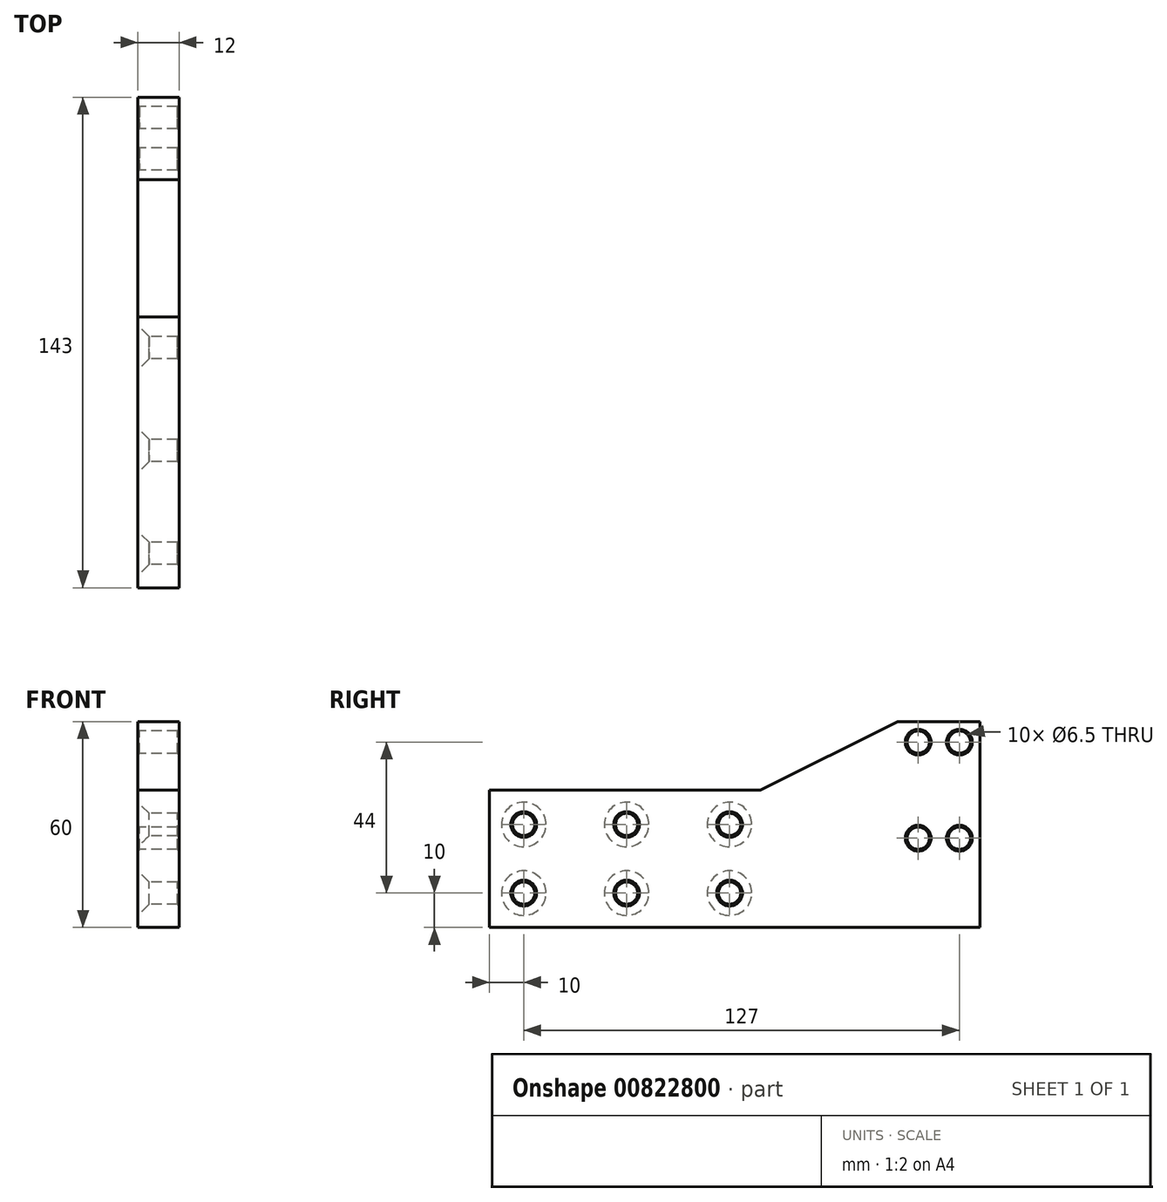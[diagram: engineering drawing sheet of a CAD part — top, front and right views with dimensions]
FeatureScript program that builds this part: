
annotation { "Feature Type Name" : "Feature", "Feature Type Description" : "" }
export const myFeature = defineFeature(function(context is Context, id is Id, definition is map)
    precondition{}
    {
        {
            var Q0;
            Q0=qCreatedBy(makeId("Right.planeOp"),FACE);
            var sketch = newSketch(context, id + "F0", { "sketchPlane" : qUnion([Q0])});
            skLineSegment(sketch, "E0.bottom", {"start": v(-71.5, 20) * mm, "end": v(7.5, 20) * mm});
            skLineSegment(sketch, "E0.top", {"start": v(-71.5, -20) * mm, "end": v(71.5, -20) * mm});
            skLineSegment(sketch, "E0.left", {"start": v(-71.5, 20) * mm, "end": v(-71.5, -20) * mm});
            skLineSegment(sketch, "E0.right", {"start": v(71.5, 20) * mm, "end": v(71.5, -20) * mm});
            skPoint(sketch, "E0.middle", {"position": v(0, 0) * mm});
            skCircle(sketch, "E1", {"center": v(-61.5, 10) * mm, "radius": 3.25 * mm});
            skLineSegment(sketch, "E2", {"start": v(-61.5, 10) * mm, "end": v(-1.5, 10) * mm, "construction": true});
            skCircle(sketch, "E3", {"center": v(-1.5, 10) * mm, "radius": 3.25 * mm});
            skCircle(sketch, "E4", {"center": v(-31.5, 10) * mm, "radius": 3.25 * mm});
            skLineSegment(sketch, "E5", {"start": v(0, 0) * mm, "end": v(-27.42, 0) * mm, "construction": true});
            skCircle(sketch, "E6.MirrorC", {"center": v(-1.5, -10) * mm, "radius": 3.25 * mm});
            skCircle(sketch, "E7.MirrorC", {"center": v(-31.5, -10) * mm, "radius": 3.25 * mm});
            skCircle(sketch, "E8.MirrorC", {"center": v(-61.5, -10) * mm, "radius": 3.25 * mm});
            skLineSegment(sketch, "E9.3", {"start": v(65.5, 34) * mm, "end": v(65.5, 6) * mm, "construction": true});
            skLineSegment(sketch, "E10", {"start": v(47.5, 20) * mm, "end": v(47.5, -20) * mm, "construction": true});
            skCircle(sketch, "E11", {"center": v(65.5, 34) * mm, "radius": 3.25 * mm});
            skCircle(sketch, "E12", {"center": v(53.5, 34) * mm, "radius": 3.25 * mm});
            skCircle(sketch, "E13", {"center": v(53.5, 6) * mm, "radius": 3.25 * mm});
            skCircle(sketch, "E14", {"center": v(65.5, 6) * mm, "radius": 3.25 * mm});
            skLineSegment(sketch, "E15", {"start": v(71.5, 20) * mm, "end": v(71.5, 40) * mm});
            skLineSegment(sketch, "E16", {"start": v(71.5, 40) * mm, "end": v(47.5, 40) * mm});
            skLineSegment(sketch, "E17", {"start": v(47.5, 40) * mm, "end": v(7.5, 20) * mm});
            skLineSegment(sketch, "E18", {"start": v(65.5, 6) * mm, "end": v(53.5, 6) * mm, "construction": true});
            skLineSegment(sketch, "E19", {"start": v(65.5, 34) * mm, "end": v(53.5, 34) * mm, "construction": true});
            skLineSegment(sketch, "E20", {"start": v(53.5, 6) * mm, "end": v(53.5, 34) * mm, "construction": true});
            skSolve(sketch);
        }
        {
            var Q0;
            Q0=qSketchRegion(id+"F0",true);
            extrude(context, id + "F1", {"entities" : qUnion([Q0]), "depth" : 12 * mm, "offsetDistance" : 25 * mm});
        }
        {
            var Q0;
            Q0=makeQuery(id+"F1.opExtrude","CAP_EDGE",EDGE,{"disambiguationData":[OSD([sQuery(id+"F0.wireOp",EDGE,"E3")])],"isStart":true});
            var Q1;
            Q1=makeQuery(id+"F1.opExtrude","CAP_EDGE",EDGE,{"disambiguationData":[OSD([sQuery(id+"F0.wireOp",EDGE,"E6.MirrorC")])],"isStart":true});
            var Q2;
            Q2=makeQuery(id+"F1.opExtrude","CAP_EDGE",EDGE,{"disambiguationData":[OSD([sQuery(id+"F0.wireOp",EDGE,"E7.MirrorC")])],"isStart":true});
            var Q3;
            Q3=makeQuery(id+"F1.opExtrude","CAP_EDGE",EDGE,{"disambiguationData":[OSD([sQuery(id+"F0.wireOp",EDGE,"E4")])],"isStart":true});
            var Q4;
            Q4=makeQuery(id+"F1.opExtrude","CAP_EDGE",EDGE,{"disambiguationData":[OSD([sQuery(id+"F0.wireOp",EDGE,"E8.MirrorC")])],"isStart":true});
            var Q5;
            Q5=makeQuery(id+"F1.opExtrude","CAP_EDGE",EDGE,{"disambiguationData":[OSD([sQuery(id+"F0.wireOp",EDGE,"E1")])],"isStart":true});
            chamfer(context, id + "F2", {"entities" : qUnion([Q0, Q1, Q2, Q3, Q4, Q5]), "width" : 3.25 * mm, "tangentPropagation" : true});
        }
        {
            var Q0;
            Q0=makeQuery(id+"F1.opExtrude","SWEPT_FACE",FACE,{"disambiguationData":[OSD([sQuery(id+"F0.wireOp",EDGE,"E11")])]});
            var Q1;
            Q1=makeQuery(id+"F1.opExtrude","SWEPT_FACE",FACE,{"disambiguationData":[OSD([sQuery(id+"F0.wireOp",EDGE,"E12")])]});
            var Q2;
            Q2=makeQuery(id+"F1.opExtrude","SWEPT_FACE",FACE,{"disambiguationData":[OSD([sQuery(id+"F0.wireOp",EDGE,"E13")])]});
            var Q3;
            Q3=makeQuery(id+"F1.opExtrude","SWEPT_FACE",FACE,{"disambiguationData":[OSD([sQuery(id+"F0.wireOp",EDGE,"E14")])]});
            var Q4;
            Q4=makeQuery(id+"F1.opExtrude","CAP_EDGE",EDGE,{"disambiguationData":[OSD([sQuery(id+"F0.wireOp",EDGE,"E1")])],"isStart":false});
            var Q5;
            Q5=makeQuery(id+"F1.opExtrude","CAP_EDGE",EDGE,{"disambiguationData":[OSD([sQuery(id+"F0.wireOp",EDGE,"E4")])],"isStart":false});
            var Q6;
            Q6=makeQuery(id+"F1.opExtrude","CAP_EDGE",EDGE,{"disambiguationData":[OSD([sQuery(id+"F0.wireOp",EDGE,"E3")])],"isStart":false});
            var Q7;
            Q7=makeQuery(id+"F1.opExtrude","CAP_EDGE",EDGE,{"disambiguationData":[OSD([sQuery(id+"F0.wireOp",EDGE,"E6.MirrorC")])],"isStart":false});
            var Q8;
            Q8=makeQuery(id+"F1.opExtrude","CAP_EDGE",EDGE,{"disambiguationData":[OSD([sQuery(id+"F0.wireOp",EDGE,"E7.MirrorC")])],"isStart":false});
            var Q9;
            Q9=makeQuery(id+"F1.opExtrude","CAP_EDGE",EDGE,{"disambiguationData":[OSD([sQuery(id+"F0.wireOp",EDGE,"E8.MirrorC")])],"isStart":false});
            chamfer(context, id + "F3", {"entities" : qUnion([Q0, Q1, Q2, Q3, Q4, Q5, Q6, Q7, Q8, Q9]), "width" : 0.5 * mm, "tangentPropagation" : true});
        }
    });
